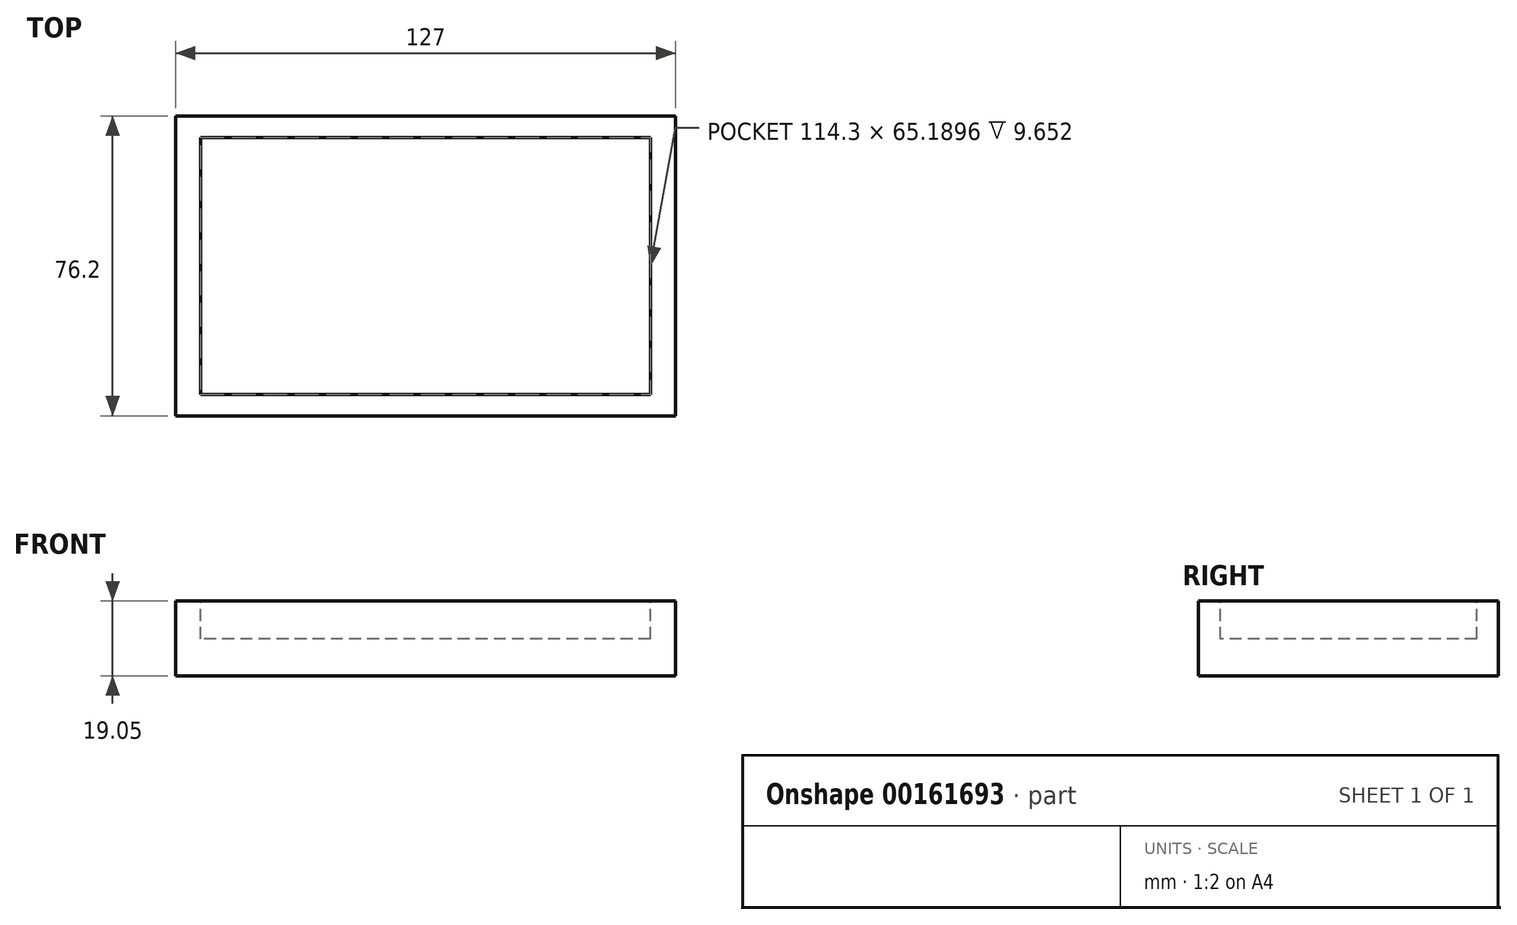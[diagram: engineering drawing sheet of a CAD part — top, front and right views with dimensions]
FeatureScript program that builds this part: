
annotation { "Feature Type Name" : "Feature", "Feature Type Description" : "" }
export const myFeature = defineFeature(function(context is Context, id is Id, definition is map)
    precondition{}
    {
        {
            var Q0;
            Q0=qCreatedBy(makeId("Top.planeOp"),FACE);
            var sketch = newSketch(context, id + "F0", { "sketchPlane" : qUnion([Q0])});
            skLineSegment(sketch, "E0.bottom", {"start": v(63.5, 38.1) * mm, "end": v(-63.5, 38.1) * mm});
            skLineSegment(sketch, "E0.top", {"start": v(63.5, -38.1) * mm, "end": v(-63.5, -38.1) * mm});
            skLineSegment(sketch, "E0.left", {"start": v(63.5, 38.1) * mm, "end": v(63.5, -38.1) * mm});
            skLineSegment(sketch, "E0.right", {"start": v(-63.5, 38.1) * mm, "end": v(-63.5, -38.1) * mm});
            skPoint(sketch, "E0.middle", {"position": v(0, 0) * mm});
            skSolve(sketch);
        }
        {
            var Q0;
            Q0=makeQuery(id+"F0.imprint","IMPRINT",FACE,{"disambiguationData":[TD([[makeQuery(id+"F0.imprint","IMPRINT",EDGE,{"derivedFrom":sQuery(id+"F0.wireOp",EDGE,"E0.bottom")}),1.0]])]});
            extrude(context, id + "F1", {"entities" : qUnion([Q0]), "depth" : 19.05 * mm});
        }
        {
            var Q0;
            Q0=makeQuery(id+"F1.opExtrude","CAP_FACE",FACE,{"disambiguationData":[OSD([sQuery(id+"F0.wireOp",EDGE,"E0.bottom"),sQuery(id+"F0.wireOp",EDGE,"E0.top"),sQuery(id+"F0.wireOp",EDGE,"E0.left"),sQuery(id+"F0.wireOp",EDGE,"E0.right")])],"isStart":false});
            var sketch = newSketch(context, id + "F2", { "sketchPlane" : qUnion([Q0])});
            skLineSegment(sketch, "E1.bottom", {"start": v(57.15, 32.6) * mm, "end": v(-57.15, 32.6) * mm});
            skLineSegment(sketch, "E1.top", {"start": v(57.15, -32.6) * mm, "end": v(-57.15, -32.6) * mm});
            skLineSegment(sketch, "E1.left", {"start": v(57.15, 32.6) * mm, "end": v(57.15, -32.6) * mm});
            skLineSegment(sketch, "E1.right", {"start": v(-57.15, 32.6) * mm, "end": v(-57.15, -32.6) * mm});
            skPoint(sketch, "E1.middle", {"position": v(0, 0) * mm});
            skLineSegment(sketch, "E2.bottom", {"start": v(-57.15, -32.6) * mm, "end": v(57.15, -32.6) * mm});
            skLineSegment(sketch, "E2.top", {"start": v(-57.15, -68.56) * mm, "end": v(57.15, -68.56) * mm});
            skLineSegment(sketch, "E2.left", {"start": v(-57.15, -32.6) * mm, "end": v(-57.15, -68.56) * mm});
            skLineSegment(sketch, "E2.right", {"start": v(57.15, -32.6) * mm, "end": v(57.15, -68.56) * mm});
            skSolve(sketch);
        }
        {
            var Q0;
            Q0=makeQuery(id+"F2.imprint","IMPRINT",FACE,{"disambiguationData":[TD([[makeQuery(id+"F2.imprint","IMPRINT",EDGE,{"derivedFrom":sQuery(id+"F2.wireOp",EDGE,"E1.bottom")}),1.0]])]});
            var Q1;
            {var subQ0=sQuery(id+"F2.wireOp",EDGE,"E2.top");Q1=makeQuery(id+"F2.imprint","IMPRINT",FACE,{"disambiguationData":[TD([[makeQuery(id+"F2.imprint","IMPRINT",EDGE,{"derivedFrom":subQ0}),1.0]])]});}
            var Q2;
            {var subQ0=sQuery(id+"F2.wireOp",EDGE,"E2.bottom");Q2=makeQuery(id+"F2.imprint","IMPRINT",FACE,{"disambiguationData":[TD([[makeQuery(id+"F2.imprint","IMPRINT",EDGE,{"derivedFrom":subQ0}),-1.0]])]});}
            extrude(context, id + "F3", {"entities" : qUnion([Q0, Q1, Q2]), "operationType" : NewBodyOperationType.REMOVE, "oppositeDirection" : true, "depth" : 9.65 * mm});
        }
    });
